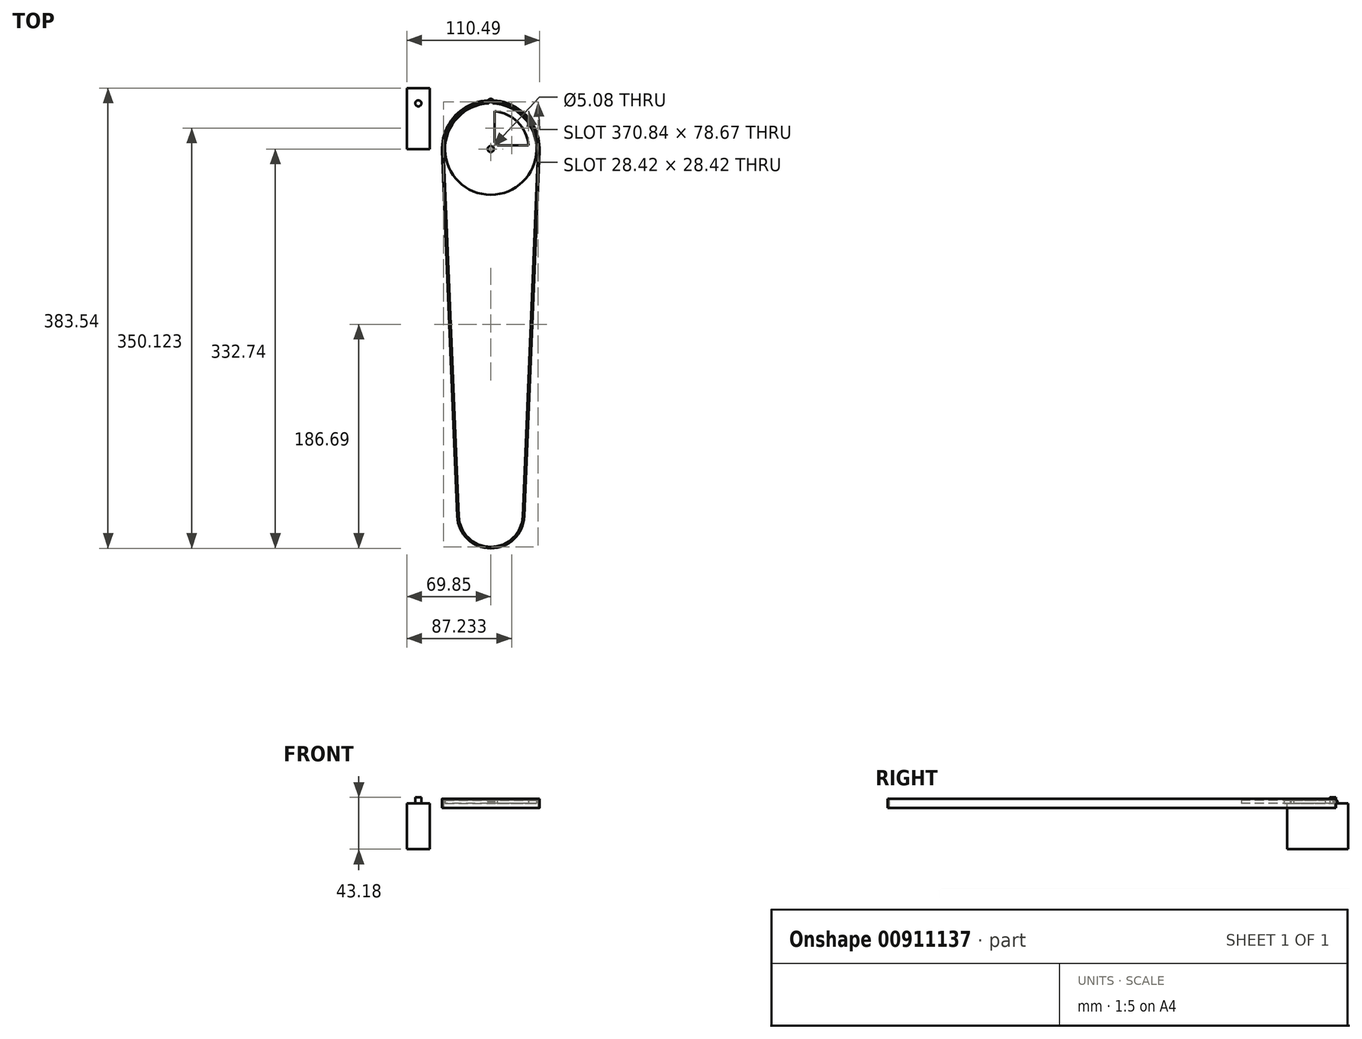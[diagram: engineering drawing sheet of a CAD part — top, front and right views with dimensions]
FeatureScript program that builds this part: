
annotation { "Feature Type Name" : "Feature", "Feature Type Description" : "" }
export const myFeature = defineFeature(function(context is Context, id is Id, definition is map)
    precondition{}
    {
        {
            var Q0;
            Q0=qCreatedBy(makeId("Top.planeOp"),FACE);
            var sketch = newSketch(context, id + "F0", { "sketchPlane" : qUnion([Q0])});
            skCircle(sketch, "E0", {"center": v(0, 0) * mm, "radius": 38.1 * mm});
            skCircle(sketch, "E1", {"center": v(0, 0) * mm, "radius": 2.54 * mm});
            skSolve(sketch);
        }
        {
            var Q0;
            Q0=makeQuery(id+"F0.imprint","IMPRINT",FACE,{"disambiguationData":[TD([[makeQuery(id+"F0.imprint","IMPRINT",EDGE,{"derivedFrom":sQuery(id+"F0.wireOp",EDGE,"E1")}),-1.0]])]});
            var Q1;
            {var subQ5=sQuery(id+"F0.wireOp",EDGE,"pq5Jjkm7-a4fV-90wC-CFVI-NsJcmO3FdSo2.bottom");Q1=makeQuery(id+"F0.imprint","IMPRINT",FACE,{"disambiguationData":[TD([[makeQuery(id+"F0.imprint","IMPRINT",EDGE,{"derivedFrom":subQ5}),1.0]])]});}
            extrude(context, id + "F1", {"entities" : qUnion([Q0, Q1]), "depth" : 2.54 * mm, "offsetDistance" : 25.4 * mm});
        }
        {
            var Q0;
            Q0=qCreatedBy(makeId("Top.planeOp"),FACE);
            var sketch = newSketch(context, id + "F2", { "sketchPlane" : qUnion([Q0])});
            skLineSegment(sketch, "E2.MirrorCS", {"start": v(1.27, 41.86) * mm, "end": v(0, 41.86) * mm});
            skLineSegment(sketch, "E3.MirrorCS", {"start": v(2.03, 38.05) * mm, "end": v(1.27, 41.86) * mm});
            skCircle(sketch, "E4.0", {"center": v(0, 0) * mm, "radius": 38.1 * mm});
            skLineSegment(sketch, "E5.MirrorCS", {"start": v(-1.27, 41.86) * mm, "end": v(0, 41.86) * mm});
            skLineSegment(sketch, "E6.MirrorCS", {"start": v(-2.03, 38.05) * mm, "end": v(-1.27, 41.86) * mm});
            skSolve(sketch);
        }
        {
            var Q0;
            Q0 = qSketchRegion(id + "F2", true);
            var Q1;
            Q1=makeQuery(id+"F1.opExtrude","CAP_FACE",FACE,{"disambiguationData":[OSD([sQuery(id+"F0.wireOp",EDGE,"E0"),sQuery(id+"F0.wireOp",EDGE,"E1")])],"isStart":false});
            extrude(context, id + "F3", {"entities" : qUnion([Q0]), "operationType" : NewBodyOperationType.ADD, "endBound" : BoundingType.UP_TO_SURFACE, "depth" : 2.54 * mm, "endBoundEntityFace" : qUnion([Q1]), "offsetDistance" : 25.4 * mm});
        }
        {
            var Q0;
            Q0=makeQuery(id+"F3.opExtrude","CAP_EDGE",EDGE,{"disambiguationData":[OSD([sQuery(id+"F2.wireOp",EDGE,"E6.MirrorCS")])],"isStart":false});
            var Q1;
            Q1=makeQuery(id+"F3.opExtrude","CAP_EDGE",EDGE,{"disambiguationData":[OSD([sQuery(id+"F2.wireOp",EDGE,"E3.MirrorCS")])],"isStart":false});
            var Q2;
            Q2=makeQuery(id+"F3.opExtrude","CAP_EDGE",EDGE,{"disambiguationData":[OSD([sQuery(id+"F2.wireOp",EDGE,"E6.MirrorCS")])],"isStart":true});
            var Q3;
            Q3=makeQuery(id+"F3.opExtrude","CAP_EDGE",EDGE,{"disambiguationData":[OSD([sQuery(id+"F2.wireOp",EDGE,"E3.MirrorCS")])],"isStart":true});
            var Q4;
            Q4=makeQuery(id+"F3.opExtrude","SWEPT_EDGE",EDGE,{"disambiguationData":[OSD([sQuery(id+"F2.wireOp",EDGE,"E2.MirrorCS"),sQuery(id+"F2.wireOp",EDGE,"E3.MirrorCS")])]});
            var Q5;
            Q5=makeQuery(id+"F3.opExtrude","CAP_EDGE",EDGE,{"disambiguationData":[OSD([sQuery(id+"F2.wireOp",EDGE,"E2.MirrorCS"),sQuery(id+"F2.wireOp",EDGE,"E5.MirrorCS")])],"isStart":false});
            var Q6;
            Q6=makeQuery(id+"F3.opExtrude","SWEPT_EDGE",EDGE,{"disambiguationData":[OSD([sQuery(id+"F2.wireOp",EDGE,"E5.MirrorCS"),sQuery(id+"F2.wireOp",EDGE,"E6.MirrorCS")])]});
            var Q7;
            Q7=makeQuery(id+"F3.opExtrude","CAP_EDGE",EDGE,{"disambiguationData":[OSD([sQuery(id+"F2.wireOp",EDGE,"E2.MirrorCS"),sQuery(id+"F2.wireOp",EDGE,"E5.MirrorCS")])],"isStart":true});
            chamfer(context, id + "F4", {"entities" : qUnion([Q0, Q1, Q2, Q3, Q4, Q5, Q6, Q7]), "width" : 0.5 * mm, "tangentPropagation" : true});
        }
        {
            var Q0;
            Q0=makeQuery(id+"F0.imprint","IMPRINT",FACE,{"disambiguationData":[TD([[makeQuery(id+"F0.imprint","IMPRINT",EDGE,{"derivedFrom":sQuery(id+"F0.wireOp",EDGE,"E1")}),1.0]])]});
            extrude(context, id + "F5", {"entities" : qUnion([Q0]), "operationType" : NewBodyOperationType.REMOVE, "endBound" : BoundingType.THROUGH_ALL, "depth" : 25.4 * mm, "offsetDistance" : 25.4 * mm});
        }
        {
            var Q0;
            Q0=qCreatedBy(makeId("Top.planeOp"),FACE);
            var sketch = newSketch(context, id + "F6", { "sketchPlane" : qUnion([Q0])});
            skLineSegment(sketch, "E7", {"start": v(3.17, 31.6) * mm, "end": v(3.18, 5.5) * mm});
            skLineSegment(sketch, "E8", {"start": v(5.5, 3.17) * mm, "end": v(31.6, 3.18) * mm});
            skArc(sketch, "E9", {"start": v(31.6, 3.18) * mm, "mid": v(22.45, 22.45) * mm, "end": v(3.18, 31.6) * mm});
            skArc(sketch, "E10", {"start": v(5.5, 3.17) * mm, "mid": v(4.5, 4.5) * mm, "end": v(3.18, 5.5) * mm});
            skSolve(sketch);
        }
        {
            var Q0;
            Q0=makeQuery(id+"F6.imprint","IMPRINT",FACE,{"disambiguationData":[TD([[makeQuery(id+"F6.imprint","IMPRINT",EDGE,{"derivedFrom":sQuery(id+"F6.wireOp",EDGE,"E7")}),1.0]])]});
            extrude(context, id + "F7", {"entities" : qUnion([Q0]), "operationType" : NewBodyOperationType.REMOVE, "endBound" : BoundingType.THROUGH_ALL, "depth" : 25.4 * mm, "offsetDistance" : 25.4 * mm});
        }
        {
            var Q0;
            Q0=qCreatedBy(makeId("Top.planeOp"),FACE);
            var sketch = newSketch(context, id + "F8", { "sketchPlane" : qUnion([Q0])});
            skLineSegment(sketch, "E11.bottom", {"start": v(-69.85, 0) * mm, "end": v(-50.8, 0) * mm});
            skLineSegment(sketch, "E11.top", {"start": v(-69.85, 50.8) * mm, "end": v(-50.8, 50.8) * mm});
            skLineSegment(sketch, "E11.left", {"start": v(-69.85, 0) * mm, "end": v(-69.85, 50.8) * mm});
            skLineSegment(sketch, "E11.right", {"start": v(-50.8, 0) * mm, "end": v(-50.8, 50.8) * mm});
            skCircle(sketch, "E12", {"center": v(-60.33, 38.1) * mm, "radius": 2.54 * mm});
            skSolve(sketch);
        }
        {
            var Q0;
            Q0=makeQuery(id+"F8.imprint","IMPRINT",FACE,{"disambiguationData":[TD([[makeQuery(id+"F8.imprint","IMPRINT",EDGE,{"derivedFrom":sQuery(id+"F8.wireOp",EDGE,"E12")}),1.0]])]});
            var Q1;
            Q1=makeQuery(id+"F8.imprint","IMPRINT",FACE,{"disambiguationData":[TD([[makeQuery(id+"F8.imprint","IMPRINT",EDGE,{"derivedFrom":sQuery(id+"F8.wireOp",EDGE,"E11.bottom")}),1.0]])]});
            extrude(context, id + "F9", {"entities" : qUnion([Q0, Q1]), "oppositeDirection" : true, "depth" : 38.1 * mm, "offsetDistance" : 25.4 * mm});
        }
        {
            var Q0;
            Q0=makeQuery(id+"F8.imprint","IMPRINT",FACE,{"disambiguationData":[TD([[makeQuery(id+"F8.imprint","IMPRINT",EDGE,{"derivedFrom":sQuery(id+"F8.wireOp",EDGE,"E12")}),1.0]])]});
            extrude(context, id + "F10", {"entities" : qUnion([Q0]), "operationType" : NewBodyOperationType.ADD, "depth" : 5.08 * mm, "offsetDistance" : 25.4 * mm});
        }
        {
            var Q0;
            Q0=qCreatedBy(makeId("Top.planeOp"),FACE);
            var sketch = newSketch(context, id + "F11", { "sketchPlane" : qUnion([Q0])});
            skArc(sketch, "E13", {"start": v(39.34, -1.64) * mm, "mid": v(0, 39.37) * mm, "end": v(-39.34, -1.64) * mm});
            skArc(sketch, "E14", {"start": v(40.6, -1.7) * mm, "mid": v(0, 40.64) * mm, "end": v(-40.6, -1.7) * mm});
            skArc(sketch, "E15", {"start": v(-26.65, -305.91) * mm, "mid": v(0, -331.47) * mm, "end": v(26.65, -305.91) * mm});
            skArc(sketch, "E16", {"start": v(-27.92, -305.96) * mm, "mid": v(0, -332.74) * mm, "end": v(27.92, -305.96) * mm});
            skLineSegment(sketch, "E17", {"start": v(40.6, -1.7) * mm, "end": v(27.92, -305.96) * mm});
            skLineSegment(sketch, "E18", {"start": v(-40.6, -1.7) * mm, "end": v(-27.92, -305.96) * mm});
            skLineSegment(sketch, "E19", {"start": v(39.34, -1.64) * mm, "end": v(26.65, -305.91) * mm});
            skLineSegment(sketch, "E20", {"start": v(-39.34, -1.64) * mm, "end": v(-26.65, -305.91) * mm});
            skSolve(sketch);
        }
        {
            var Q0;
            Q0=makeQuery(id+"F11.imprint","IMPRINT",FACE,{"disambiguationData":[TD([[makeQuery(id+"F11.imprint","IMPRINT",EDGE,{"derivedFrom":sQuery(id+"F11.wireOp",EDGE,"E13")}),-1.0]])]});
            extrude(context, id + "F12", {"entities" : qUnion([Q0]), "depth" : 7.62 * mm, "offsetDistance" : 25.4 * mm, "symmetric" : true});
        }
    });
